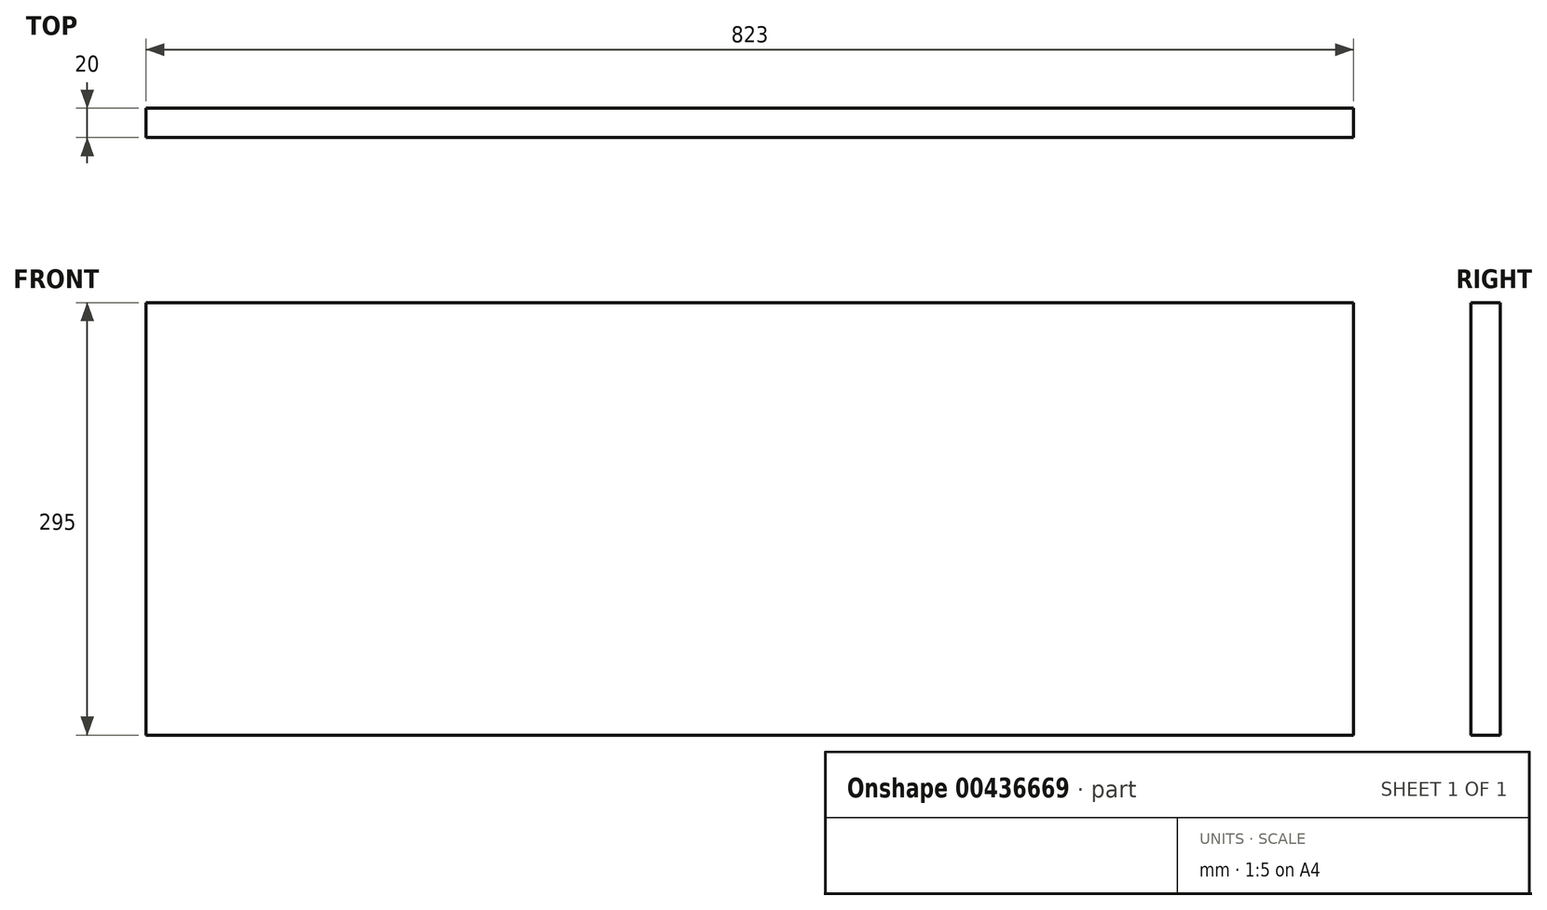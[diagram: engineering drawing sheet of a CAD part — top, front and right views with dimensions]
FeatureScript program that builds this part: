
annotation { "Feature Type Name" : "Feature", "Feature Type Description" : "" }
export const myFeature = defineFeature(function(context is Context, id is Id, definition is map)
    precondition{}
    {
        {
            var Q0;
            Q0=qCreatedBy(makeId("Front.planeOp"),FACE);
            var sketch = newSketch(context, id + "F0", { "sketchPlane" : qUnion([Q0])});
            skLineSegment(sketch, "E0.bottom", {"start": v(411.5, 147.5) * mm, "end": v(-411.5, 147.5) * mm});
            skLineSegment(sketch, "E0.top", {"start": v(411.5, -147.5) * mm, "end": v(-411.5, -147.5) * mm});
            skLineSegment(sketch, "E0.left", {"start": v(411.5, 147.5) * mm, "end": v(411.5, -147.5) * mm});
            skLineSegment(sketch, "E0.right", {"start": v(-411.5, 147.5) * mm, "end": v(-411.5, -147.5) * mm});
            skPoint(sketch, "E0.middle", {"position": v(0, 0) * mm});
            skSolve(sketch);
        }
        {
            var Q0;
            Q0=qSketchRegion(id+"F0",true);
            extrude(context, id + "F1", {"entities" : qUnion([Q0]), "depth" : 20 * mm});
        }
    });
